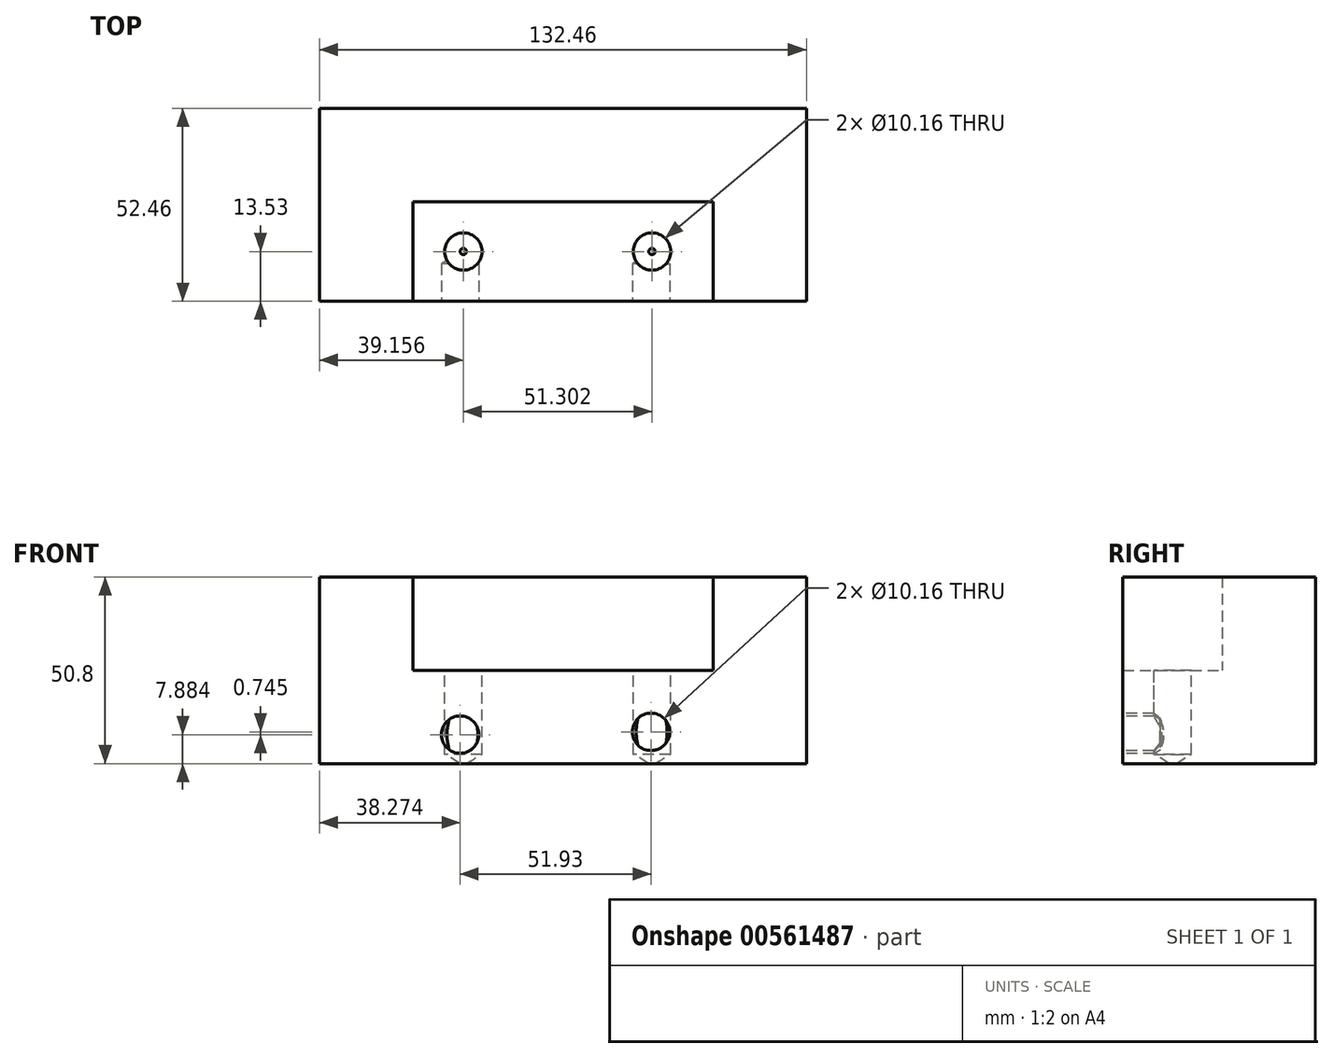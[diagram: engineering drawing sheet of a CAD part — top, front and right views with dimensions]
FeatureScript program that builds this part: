
annotation { "Feature Type Name" : "Feature", "Feature Type Description" : "" }
export const myFeature = defineFeature(function(context is Context, id is Id, definition is map)
    precondition{}
    {
        {
            var Q0;
            Q0=qCreatedBy(makeId("Top.planeOp"),FACE);
            var sketch = newSketch(context, id + "F0", { "sketchPlane" : qUnion([Q0])});
            skLineSegment(sketch, "E0.bottom", {"start": v(66.23, -26.23) * mm, "end": v(-66.23, -26.23) * mm});
            skLineSegment(sketch, "E0.top", {"start": v(66.23, 26.23) * mm, "end": v(-66.23, 26.23) * mm});
            skLineSegment(sketch, "E0.left", {"start": v(66.23, -26.23) * mm, "end": v(66.23, 26.23) * mm});
            skLineSegment(sketch, "E0.right", {"start": v(-66.23, -26.23) * mm, "end": v(-66.23, 26.23) * mm});
            skPoint(sketch, "E0.middle", {"position": v(0, 0) * mm});
            skSolve(sketch);
        }
        {
            var Q0;
            Q0=makeQuery(id+"F0.imprint","IMPRINT",FACE,{"disambiguationData":[TD([[makeQuery(id+"F0.imprint","IMPRINT",EDGE,{"derivedFrom":sQuery(id+"F0.wireOp",EDGE,"E0.bottom")}),-1.0]])]});
            extrude(context, id + "F1", {"entities" : qUnion([Q0]), "depth" : 25.4 * mm, "offsetDistance" : 25.4 * mm});
        }
        {
            var Q0;
            Q0=makeQuery(id+"F1.opExtrude","CAP_FACE",FACE,{"disambiguationData":[OSD([sQuery(id+"F0.wireOp",EDGE,"E0.bottom"),sQuery(id+"F0.wireOp",EDGE,"E0.top"),sQuery(id+"F0.wireOp",EDGE,"E0.left"),sQuery(id+"F0.wireOp",EDGE,"E0.right")])],"isStart":true});
            extrude(context, id + "F2", {"entities" : qUnion([Q0]), "operationType" : NewBodyOperationType.ADD, "depth" : 25.4 * mm, "offsetDistance" : 25.4 * mm});
        }
        {
            var Q0;
            Q0=makeQuery(id+"F1.opExtrude","CAP_FACE",FACE,{"disambiguationData":[OSD([sQuery(id+"F0.wireOp",EDGE,"E0.bottom"),sQuery(id+"F0.wireOp",EDGE,"E0.top"),sQuery(id+"F0.wireOp",EDGE,"E0.left"),sQuery(id+"F0.wireOp",EDGE,"E0.right")])],"isStart":false});
            var Q1;
            {var subQ0=sQuery(id+"F0.wireOp",EDGE,"E0.bottom");Q1=makeQuery(id+"F2.boolean.opBoolean","MERGE",FACE,{"derivedFrom":[makeQuery(id+"F1.opExtrude","SWEPT_FACE",FACE,{"disambiguationData":[OSD([subQ0])]}),makeQuery(id+"F2.opExtrude","SWEPT_FACE",FACE,{"disambiguationData":[OSD([subQ0])]})]});}
            shell(context, id + "F3", {"entities" : qUnion([Q0, Q1]), "thickness" : 25.4 * mm});
        }
        {
            var Q0;
            Q0=makeQuery(id+"F3.opShell","OFFSET_FACE",FACE,{"disambiguationData":[OSD([sQuery(id+"F0.wireOp",EDGE,"E0.bottom"),sQuery(id+"F0.wireOp",EDGE,"E0.top"),sQuery(id+"F0.wireOp",EDGE,"E0.left"),sQuery(id+"F0.wireOp",EDGE,"E0.right")])]});
            var sketch = newSketch(context, id + "F4", { "sketchPlane" : qUnion([Q0])});
            skCircle(sketch, "E1", {"center": v(-27.07, -12.7) * mm, "radius": 10.48 * mm});
            skPoint(sketch, "E1.centerSnap0", {"position": v(-40.83, -12.7) * mm});
            skCircle(sketch, "E2", {"center": v(24.23, -12.7) * mm, "radius": 9.92 * mm});
            skSolve(sketch);
        }
        {
            var Q0;
            Q0=sQuery(id+"F4.wireOp",VERTEX,"E2.center");
            var Q1;
            Q1=sQuery(id+"F4.wireOp",VERTEX,"E1.center");
            var Q2;
            Q2=makeQuery(id+"F1.opExtrude","SWEPT_BODY",BODY,{"disambiguationData":[OSD([sQuery(id+"F0.wireOp",EDGE,"E0.bottom"),sQuery(id+"F0.wireOp",EDGE,"E0.top"),sQuery(id+"F0.wireOp",EDGE,"E0.left"),sQuery(id+"F0.wireOp",EDGE,"E0.right")])]});
            hole(context, id + "F5", {"style" : HoleStyle.SIMPLE, "endStyle" : HoleEndStyle.BLIND, "holeDiameter" : 10.16 * mm, "holeDepth" : 22.86 * mm, "isTappedThrough" : true, "tappedDepth" : 12.7 * mm, "tapClearance" : 3, "startFromSketch" : true, "locations" : qUnion([Q0, Q1]), "scope" : qUnion([Q2])});
        }
        {
            var Q0;
            {var subQ0=sQuery(id+"F0.wireOp",EDGE,"E0.bottom");Q0=makeQuery(id+"F2.boolean.opBoolean","MERGE",FACE,{"derivedFrom":[makeQuery(id+"F1.opExtrude","SWEPT_FACE",FACE,{"disambiguationData":[OSD([subQ0])]}),makeQuery(id+"F2.opExtrude","SWEPT_FACE",FACE,{"disambiguationData":[OSD([subQ0])]})]});}
            var sketch = newSketch(context, id + "F6", { "sketchPlane" : qUnion([Q0])});
            skCircle(sketch, "E3", {"center": v(-27.96, -17.52) * mm, "radius": 3.86 * mm});
            skCircle(sketch, "E4", {"center": v(23.97, -16.77) * mm, "radius": 3.35 * mm});
            skSolve(sketch);
        }
        {
            var Q0;
            Q0=sQuery(id+"F6.wireOp",VERTEX,"E3.center");
            var Q1;
            Q1=sQuery(id+"F6.wireOp",VERTEX,"E4.center");
            var Q2;
            Q2=makeQuery(id+"F1.opExtrude","SWEPT_BODY",BODY,{"disambiguationData":[OSD([sQuery(id+"F0.wireOp",EDGE,"E0.bottom"),sQuery(id+"F0.wireOp",EDGE,"E0.top"),sQuery(id+"F0.wireOp",EDGE,"E0.left"),sQuery(id+"F0.wireOp",EDGE,"E0.right")])]});
            hole(context, id + "F7", {"style" : HoleStyle.SIMPLE, "endStyle" : HoleEndStyle.BLIND, "holeDiameter" : 10.16 * mm, "holeDepth" : 10.16 * mm, "isTappedThrough" : true, "tappedDepth" : 12.7 * mm, "tapClearance" : 3, "startFromSketch" : true, "locations" : qUnion([Q0, Q1]), "scope" : qUnion([Q2])});
        }
    });
